FCSTD DOCUMENT  (FreeCAD 0.21R33771 (Git))
Label: Assemblage
License: All rights reserved
LicenseURL: https://en.wikipedia.org/wiki/All_rights_reserved
objects: App::DocumentObjectGroup×3, App::Link×3, PartDesign::CoordinateSystem×1, App::FeaturePython×1, App::Part×1
note: 1 computed .brp shape members not serialized (recipe doc carries the construction recipe); baked Part::Feature solids carry a one-line shape summary decoded from their .brp
EXTERNAL_REF file=servomoteur.FCStd obj=FS5109M_Ensemble_servo
EXTERNAL_REF file=support_servomoteur.FCStd obj=Body
EXTERNAL_REF file=levier.FCStd obj=Body002

FEATURE [App::DocumentObjectGroup] Parts
FEATURE [PartDesign::CoordinateSystem] LCS_Origin
  AttacherType = Attacher::AttachEngine3D
  MapMode = 2
  Support = -> [X_Axis]
FEATURE [App::DocumentObjectGroup] Constraints
FEATURE [App::FeaturePython] Variables  # WARN: FeaturePython — macro-defined, semantics opaque (R4)
  Type = App::PropertyContainer
FEATURE [App::DocumentObjectGroup] Configurations
FEATURE [App::Link] FS5109M_Ensemble_servo  label="FS5109M_Ensemble servo"
  LinkPlacement = pos=(1.25,-0.24999,62) rot=(1,0,0;1.5708rad)
  LinkedObject = -> <external servomoteur.FCStd>#FS5109M_Ensemble_servo
  Placement = pos=(1.25,-0.24999,62) rot=(1,0,0;1.5708rad)
FEATURE [App::Link] Support
  LinkedObject = -> <external support_servomoteur.FCStd>#Body
FEATURE [App::Link] Levier
  LinkPlacement = pos=(11.25,-0.250031,86.5) rot=(0.707107,0.707107,0;3.14159rad)
  LinkedObject = -> <external levier.FCStd>#Body002
  Placement = pos=(11.25,-0.250031,86.5) rot=(0.707107,0.707107,0;3.14159rad)
FEATURE [App::Part] Assembly
  AssemblyType = Part::Link
  Group = -> [LCS_Origin,Constraints,Variables,Configurations,FS5109M_Ensemble_servo,Support,Levier]
  Origin = -> Origin
  Type = Assembly

RESOLVED EXTERNAL PARTS (link-assembly join: the EXTERNAL_REF files above that resolve inside this repo's crawl, each included once):
---- part levier.FCStd = doc fcstd_0c7b5a764832 ----
FCSTD DOCUMENT  (FreeCAD 0.21R33771 (Git))
Label: levier
License: All rights reserved
LicenseURL: http://en.wikipedia.org/wiki/All_rights_reserved
objects: Sketcher::SketchObject×4, PartDesign::Pad×2, PartDesign::Pocket×2, PartDesign::Body×1
note: 13 computed .brp shape members not serialized (recipe doc carries the construction recipe); baked Part::Feature solids carry a one-line shape summary decoded from their .brp

FEATURE [Sketcher::SketchObject] Sketch001
  FullyConstrained = true
  MapMode = 5
  Support = -> [XY_Plane002]
  sketch-geometry (4):
    g0: ArcOfCircle CenterX=0 CenterY=0 CenterZ=0 NormalX=0 NormalY=0 NormalZ=1 AngleXU=0 Radius=14 StartAngle=-3.40394e-11 EndAngle=3.14159
    g1: ArcOfCircle CenterX=6.08e-14 CenterY=-42 CenterZ=0 NormalX=0 NormalY=0 NormalZ=1 AngleXU=0 Radius=14 StartAngle=3.14159 EndAngle=6.28319
    g2: LineSegment StartX=-14 StartY=2.14512e-11 StartZ=0 EndX=-14 EndY=-42 EndZ=0
    g3: LineSegment StartX=14 StartY=-42 StartZ=0 EndX=14 EndY=-4.76554e-10 EndZ=0
  constraints (9):
    c: Tangent(g0,g2) = -1.5708
    c: Tangent(g2,g1) = -1.5708
    c: Tangent(g1,g3) = -1.5708
    c: Tangent(g3,g0) = -1.5708
    c: Equal(g0,g1)
    c: Coincident(g0,g-1)
    c: Vertical(g2)
    c: Diameter(g0) = 28
    c: DistanceY(g1,g0) = 42
FEATURE [PartDesign::Pad] Pad
  Direction = (0,0,1)
  Length = 12
  Length2 = 10
  Profile = -> Sketch001
  ReferenceAxis = -> Sketch001 [N_Axis]
  Type = 0
FEATURE [Sketcher::SketchObject] Sketch
  FullyConstrained = true
  MapMode = 5
  Placement = pos=(0,0,12) rot=(0,0,1;0rad)
  Support = -> [Pad]
  sketch-geometry (6):
    g0: ArcOfCircle CenterX=0 CenterY=0 CenterZ=0 NormalX=0 NormalY=0 NormalZ=1 AngleXU=0 Radius=7.5 StartAngle=5.63968 EndAngle=10.0683
    g1: LineSegment StartX=-3.84916 StartY=-7.80612 StartZ=0 EndX=-3.84916 EndY=-23.5061 EndZ=0
    g2: LineSegment StartX=3.85084 StartY=-7.8 StartZ=0 EndX=3.85084 EndY=-23.5 EndZ=0
    g3: ArcOfCircle CenterX=0.000837628 CenterY=-23.5 CenterZ=0 NormalX=0 NormalY=0 NormalZ=1 AngleXU=0 Radius=3.85 StartAngle=3.14318 EndAngle=6.28319
    g4: ArcOfCircle CenterX=-10.1 CenterY=-9.52 CenterZ=0 NormalX=0 NormalY=0 NormalZ=1 AngleXU=0 Radius=6.48154 StartAngle=0.267608 EndAngle=0.885935
    g5: ArcOfCircle CenterX=10.1 CenterY=-9.52 CenterZ=0 NormalX=0 NormalY=0 NormalZ=1 AngleXU=0 Radius=6.48154 StartAngle=2.25566 EndAngle=2.87301
  constraints (20):
    c: Coincident(g0,g-1)
    c: Vertical(g1)
    c: Vertical(g2)
    c: Equal(g2,g1)
    c: Coincident(g3,g1)
    c: Coincident(g3,g2)
    c: DistanceX(g1,g2) = 7.7
    c: Diameter(g0) = 15
    c: DistanceY(g2,g2) = 15.7
    c: DistanceY(g3,g0) = 23.5
    c: DistanceY(g0,g0) = 4.5
    c: Horizontal(g0,g0)
    c: Coincident(g4,g0)
    c: Coincident(g4,g1)
    c: Coincident(g5,g0)
    c: Coincident(g5,g2)
    c: DistanceY(g2,g0) = 7.8
    c: Symmetric(g5,g4,g-2)
    c: DistanceY(g5,g0) = 9.52
    c: DistanceX(g0,g5) = 10.1
FEATURE [PartDesign::Pocket] Pocket
  BaseFeature = -> Pad
  Direction = (0,0,-1)
  Length = 4
  Length2 = 5
  Profile = -> Sketch
  ReferenceAxis = -> Sketch [N_Axis]
  Type = 0
FEATURE [Sketcher::SketchObject] Sketch002
  ExternalGeometry = -> [Pocket]
  FullyConstrained = true
  MapMode = 5
  Placement = pos=(0,0,0) rot=(1,0,0;3.14159rad)
  Support = -> [Pocket]
  sketch-geometry (1):
    g0: Circle CenterX=0 CenterY=42 CenterZ=0 NormalX=0 NormalY=0 NormalZ=1 AngleXU=0 Radius=5.25
  constraints (2):
    c: Coincident(g0,g-3)
    c: Diameter(g0) = 10.5
FEATURE [PartDesign::Pad] Pad001
  BaseFeature = -> Pocket
  Direction = (0,0,-1)
  Length = 20
  Length2 = 10
  Profile = -> Sketch002
  ReferenceAxis = -> Sketch002 [N_Axis]
  Type = 0
FEATURE [Sketcher::SketchObject] Sketch003
  ExternalGeometry = -> [Pad001]
  FullyConstrained = true
  MapMode = 5
  Placement = pos=(0,0,8) rot=(0,0,1;0rad)
  Support = -> [Pad001]
  sketch-geometry (2):
    g0: Circle CenterX=0 CenterY=0 CenterZ=0 NormalX=0 NormalY=0 NormalZ=1 AngleXU=0 Radius=1.4
    g1: Circle CenterX=0.000837628 CenterY=-23.5 CenterZ=0 NormalX=0 NormalY=0 NormalZ=1 AngleXU=0 Radius=1.4
  constraints (4):
    c: Coincident(g0,g-4)
    c: Coincident(g1,g-3)
    c: Diameter(g0) = 2.8
    c: Equal(g0,g1)
FEATURE [PartDesign::Pocket] Pocket001
  BaseFeature = -> Pad001
  Direction = (0,0,-1)
  Length = 5
  Length2 = 5
  Profile = -> Sketch003
  ReferenceAxis = -> Sketch003 [N_Axis]
  Type = 1
FEATURE [PartDesign::Body] Body002  label="Levier"
  Group = -> [Sketch001,Pad,Sketch,Pocket,Sketch002,Pad001,Sketch003,Pocket001]
  Origin = -> Origin002
  Tip = -> Pocket001
---- part support_servomoteur.FCStd = doc fcstd_80a353f72cd3 ----
FCSTD DOCUMENT  (FreeCAD 0.21R33771 (Git))
Label: support_servomoteur
License: All rights reserved
LicenseURL: https://en.wikipedia.org/wiki/All_rights_reserved
objects: Sketcher::SketchObject×6, PartDesign::Pad×3, PartDesign::Pocket×3, PartDesign::Fillet×1, PartDesign::Body×1
note: 21 computed .brp shape members not serialized (recipe doc carries the construction recipe); baked Part::Feature solids carry a one-line shape summary decoded from their .brp

FEATURE [Sketcher::SketchObject] Sketch
  FullyConstrained = true
  MapMode = 5
  Support = -> [XY_Plane]
  sketch-geometry (4):
    g0: LineSegment StartX=-40 StartY=-55 StartZ=0 EndX=40 EndY=-55 EndZ=0
    g1: LineSegment StartX=40 StartY=-55 StartZ=0 EndX=40 EndY=55 EndZ=0
    g2: LineSegment StartX=40 StartY=55 StartZ=0 EndX=-40 EndY=55 EndZ=0
    g3: LineSegment StartX=-40 StartY=55 StartZ=0 EndX=-40 EndY=-55 EndZ=0
  constraints (11):
    c: Coincident(g0,g1)
    c: Coincident(g1,g2)
    c: Coincident(g2,g3)
    c: Coincident(g3,g0)
    c: Horizontal(g0)
    c: Horizontal(g2)
    c: Vertical(g1)
    c: Vertical(g3)
    c: DistanceX(g2,g2) = 80
    c: DistanceY(g1,g1) = 110
    c: Symmetric(g2,g0,g-1)
FEATURE [PartDesign::Pad] Pad
  Direction = (0,0,1)
  Length = 5
  Length2 = 10
  Profile = -> Sketch
  ReferenceAxis = -> Sketch [N_Axis]
  Type = 0
FEATURE [Sketcher::SketchObject] Sketch001
  ExternalGeometry = -> [Pad]
  FullyConstrained = true
  MapMode = 5
  Placement = pos=(0,0,5) rot=(0,0,1;0rad)
  Support = -> [Pad]
  sketch-geometry (8):
    g0: LineSegment StartX=-3 StartY=49.5 StartZ=0 EndX=5 EndY=49.5 EndZ=0
    g1: LineSegment StartX=5 StartY=49.5 StartZ=0 EndX=5 EndY=46 EndZ=0
    g2: LineSegment StartX=5 StartY=46 StartZ=0 EndX=-3 EndY=46 EndZ=0
    g3: LineSegment StartX=-3 StartY=46 StartZ=0 EndX=-3 EndY=49.5 EndZ=0
    g4: LineSegment StartX=-3 StartY=-46 StartZ=0 EndX=5 EndY=-46 EndZ=0
    g5: LineSegment StartX=5 StartY=-46 StartZ=0 EndX=5 EndY=-49.5 EndZ=0
    g6: LineSegment StartX=5 StartY=-49.5 StartZ=0 EndX=-3 EndY=-49.5 EndZ=0
    g7: LineSegment StartX=-3 StartY=-49.5 StartZ=0 EndX=-3 EndY=-46 EndZ=0
  constraints (23):
    c: Coincident(g0,g1)
    c: Coincident(g1,g2)
    c: Coincident(g2,g3)
    c: Coincident(g3,g0)
    c: Horizontal(g0)
    c: Horizontal(g2)
    c: Vertical(g1)
    c: Vertical(g3)
    c: Coincident(g4,g5)
    c: Coincident(g5,g6)
    c: Coincident(g6,g7)
    c: Coincident(g7,g4)
    c: Horizontal(g4)
    c: Horizontal(g6)
    c: Vertical(g5)
    c: Vertical(g7)
    c: Equal(g1,g5)
    c: Equal(g0,g4)
    c: Symmetric(g2,g4,g-1)
    c: DistanceX(g0,g-4) = 35
    c: DistanceX(g0,g0) = 8
    c: DistanceY(g3,g3) = 3.5
    c: DistanceY(g4,g1) = 92
FEATURE [PartDesign::Pad] Pad001
  BaseFeature = -> Pad
  Direction = (0,0,1)
  Length = 20
  Length2 = 10
  Profile = -> Sketch001
  ReferenceAxis = -> Sketch001 [N_Axis]
  Type = 0
FEATURE [Sketcher::SketchObject] Sketch002
  ExternalGeometry = -> [Pad001]
  FullyConstrained = true
  MapMode = 5
  Placement = pos=(0,0,5) rot=(0,0,1;0rad)
  Support = -> [Pad001]
  sketch-geometry (4):
    g0: LineSegment StartX=-28 StartY=9 StartZ=0 EndX=31 EndY=9 EndZ=0
    g1: LineSegment StartX=31 StartY=9 StartZ=0 EndX=31 EndY=-17 EndZ=0
    g2: LineSegment StartX=31 StartY=-17 StartZ=0 EndX=-28 EndY=-17 EndZ=0
    g3: LineSegment StartX=-28 StartY=-17 StartZ=0 EndX=-28 EndY=9 EndZ=0
  constraints (12):
    c: Coincident(g0,g1)
    c: Coincident(g1,g2)
    c: Coincident(g2,g3)
    c: Coincident(g3,g0)
    c: Horizontal(g0)
    c: Horizontal(g2)
    c: Vertical(g1)
    c: Vertical(g3)
    c: DistanceX(g0,g0) = 59
    c: DistanceY(g1,g1) = 26
    c: DistanceY(g-1,g0) = 9
    c: DistanceX(g0,g-4) = 9
FEATURE [PartDesign::Pad] Pad002
  BaseFeature = -> Pad001
  Direction = (0,0,1)
  Length = 50
  Length2 = 10
  Profile = -> Sketch002
  ReferenceAxis = -> Sketch002 [N_Axis]
  Type = 0
FEATURE [Sketcher::SketchObject] Sketch003
  ExternalGeometry = -> [Pad002]
  FullyConstrained = true
  MapMode = 5
  Placement = pos=(0,0,0) rot=(1,0,0;3.14159rad)
  Support = -> [Pad002]
  sketch-geometry (4):
    g0: LineSegment StartX=21.65 StartY=14.25 StartZ=0 EndX=-18.65 EndY=14.25 EndZ=0
    g1: LineSegment StartX=-18.65 StartY=14.25 StartZ=0 EndX=-18.65 EndY=-6.25 EndZ=0
    g2: LineSegment StartX=-18.65 StartY=-6.25 StartZ=0 EndX=21.65 EndY=-6.25 EndZ=0
    g3: LineSegment StartX=21.65 StartY=-6.25 StartZ=0 EndX=21.65 EndY=14.25 EndZ=0
  constraints (14):
    c: Coincident(g0,g1)
    c: Coincident(g1,g2)
    c: Coincident(g2,g3)
    c: Coincident(g3,g0)
    c: Horizontal(g0)
    c: Horizontal(g2)
    c: Vertical(g1)
    c: Vertical(g3)
    c: DistanceX(g2,g2) = 40.3
    c: DistanceY(g3,g3) = 20.5
    c: DistanceY(g0,g-14) = 2.75
    c: DistanceX(g0,g-14) = 9.35
    c: DistanceY(g-14,g-14) = 26
    c: DistanceX(g-11,g-11) = 59
FEATURE [PartDesign::Pocket] Pocket
  BaseFeature = -> Pad002
  Direction = (0,0,1)
  Length = 50
  Length2 = 5
  Profile = -> Sketch003
  ReferenceAxis = -> Sketch003 [N_Axis]
  Type = 1
FEATURE [Sketcher::SketchObject] Sketch004
  ExternalGeometry = -> [Pocket]
  FullyConstrained = true
  MapMode = 5
  Placement = pos=(0,0,55) rot=(0,0,1;0rad)
  Support = -> [Pocket]
  sketch-geometry (8):
    g0: Circle CenterX=-23.25 CenterY=1 CenterZ=0 NormalX=0 NormalY=0 NormalZ=1 AngleXU=0 Radius=0.5
    g1: Circle CenterX=-23.25 CenterY=-9 CenterZ=0 NormalX=0 NormalY=0 NormalZ=1 AngleXU=0 Radius=0.5
    g2: Circle CenterX=26.25 CenterY=-9 CenterZ=0 NormalX=0 NormalY=0 NormalZ=1 AngleXU=0 Radius=0.5
    g3: Circle CenterX=26.25 CenterY=1 CenterZ=0 NormalX=0 NormalY=0 NormalZ=1 AngleXU=0 Radius=0.5
    g4: LineSegment StartX=26.25 StartY=1 StartZ=0 EndX=21.65 EndY=1 EndZ=0
    g5: LineSegment StartX=-23.25 StartY=1 StartZ=0 EndX=-18.65 EndY=1 EndZ=0
    g6: LineSegment StartX=26.25 StartY=1 StartZ=0 EndX=21.65 EndY=6.25 EndZ=0
    g7: LineSegment StartX=26.25 StartY=-9 StartZ=0 EndX=21.65 EndY=-14.25 EndZ=0
  constraints (22):
    c: Vertical(g3,g2)
    c: Vertical(g0,g1)
    c: Horizontal(g0,g3)
    c: Horizontal(g1,g2)
    c: Equal(g3,g2)
    c: Equal(g3,g0)
    c: Equal(g3,g1)
    c: Diameter(g3) = 1
    c: DistanceX(g0,g3) = 49.5
    c: DistanceY(g1,g0) = 10
    c: Coincident(g4,g3)
    c: PointOnObject(g4,g-5)
    c: Horizontal(g4)
    c: Coincident(g5,g0)
    c: PointOnObject(g5,g-3)
    c: Horizontal(g5)
    c: Equal(g5,g4)
    c: Coincident(g6,g3)
    c: Coincident(g6,g-5)
    c: Coincident(g7,g2)
    c: Coincident(g7,g-6)
    c: Equal(g6,g7)
FEATURE [PartDesign::Pocket] Pocket001
  BaseFeature = -> Pocket
  Direction = (0,0,-1)
  Length = 10
  Length2 = 5
  Profile = -> Sketch004
  ReferenceAxis = -> Sketch004 [N_Axis]
  Type = 0
FEATURE [Sketcher::SketchObject] Sketch006
  FullyConstrained = false
  MapMode = 5
  Placement = pos=(0,0,5) rot=(0,0,1;0rad)
  sketch-geometry (12):
    g0: LineSegment StartX=-40 StartY=16 StartZ=0 EndX=-7 EndY=34.5 EndZ=0
    g1: LineSegment StartX=8 StartY=34.5 StartZ=0 EndX=40 EndY=16 EndZ=0
    g2: LineSegment StartX=40 StartY=-14 StartZ=0 EndX=8 EndY=-55 EndZ=0
    g3: LineSegment StartX=-7 StartY=-55 StartZ=0 EndX=-40 EndY=-14 EndZ=0
    g4: LineSegment StartX=-40 StartY=16 StartZ=0 EndX=-40 EndY=55 EndZ=0
    g5: LineSegment StartX=-40 StartY=55 StartZ=0 EndX=-7 EndY=55 EndZ=0
    g6: LineSegment StartX=8 StartY=34.5 StartZ=0 EndX=40 EndY=55 EndZ=0
    g7: LineSegment StartX=40 StartY=16 StartZ=0 EndX=40 EndY=55 EndZ=0
    g8: LineSegment StartX=40 StartY=-14 StartZ=0 EndX=40 EndY=-55 EndZ=0
    g9: LineSegment StartX=40 StartY=-55 StartZ=0 EndX=8 EndY=-55 EndZ=0
    g10: LineSegment StartX=-7 StartY=-55 StartZ=0 EndX=-40 EndY=-55 EndZ=0
    g11: LineSegment StartX=-40 StartY=-14 StartZ=0 EndX=-40 EndY=-55 EndZ=0
  constraints (14):
    c: DistanceY(g2,g1) = 30
    c: DistanceX(g0,g1) = 15
    c: Vertical(g0,g3)
    c: Vertical(g1,g2)
    c: Horizontal(g1,g0)
    c: Horizontal(g2,g3)
    c: Coincident(g4,g0)
    c: Coincident(g5,g4)
    c: Coincident(g6,g1)
    c: Coincident(g7,g1)
    c: Coincident(g8,g2)
    c: Coincident(g9,g8)
    c: Coincident(g10,g3)
    c: Coincident(g11,g3)
FEATURE [PartDesign::Pocket] Pocket003
  BaseFeature = -> Pocket001
  Direction = (0,0,-1)
  Length = 5
  Length2 = 5
  Profile = -> Sketch006
  ReferenceAxis = -> Sketch006 [N_Axis]
  Type = 1
FEATURE [PartDesign::Fillet] Fillet
  Base = -> Pocket003 [Edge40,Edge39,Edge17,Edge2,Edge4,Edge36,Edge37,Edge38]
  BaseFeature = -> Pocket003
  Radius = 5
  SupportTransform = false
  UseAllEdges = false
FEATURE [PartDesign::Body] Body  label="Corps"
  Group = -> [Sketch,Pad,Sketch001,Pad001,Sketch002,Pad002,Sketch003,Pocket,Sketch004,Pocket001,Sketch006,Pocket003,Fillet]
  Origin = -> Origin
  Tip = -> Fillet
